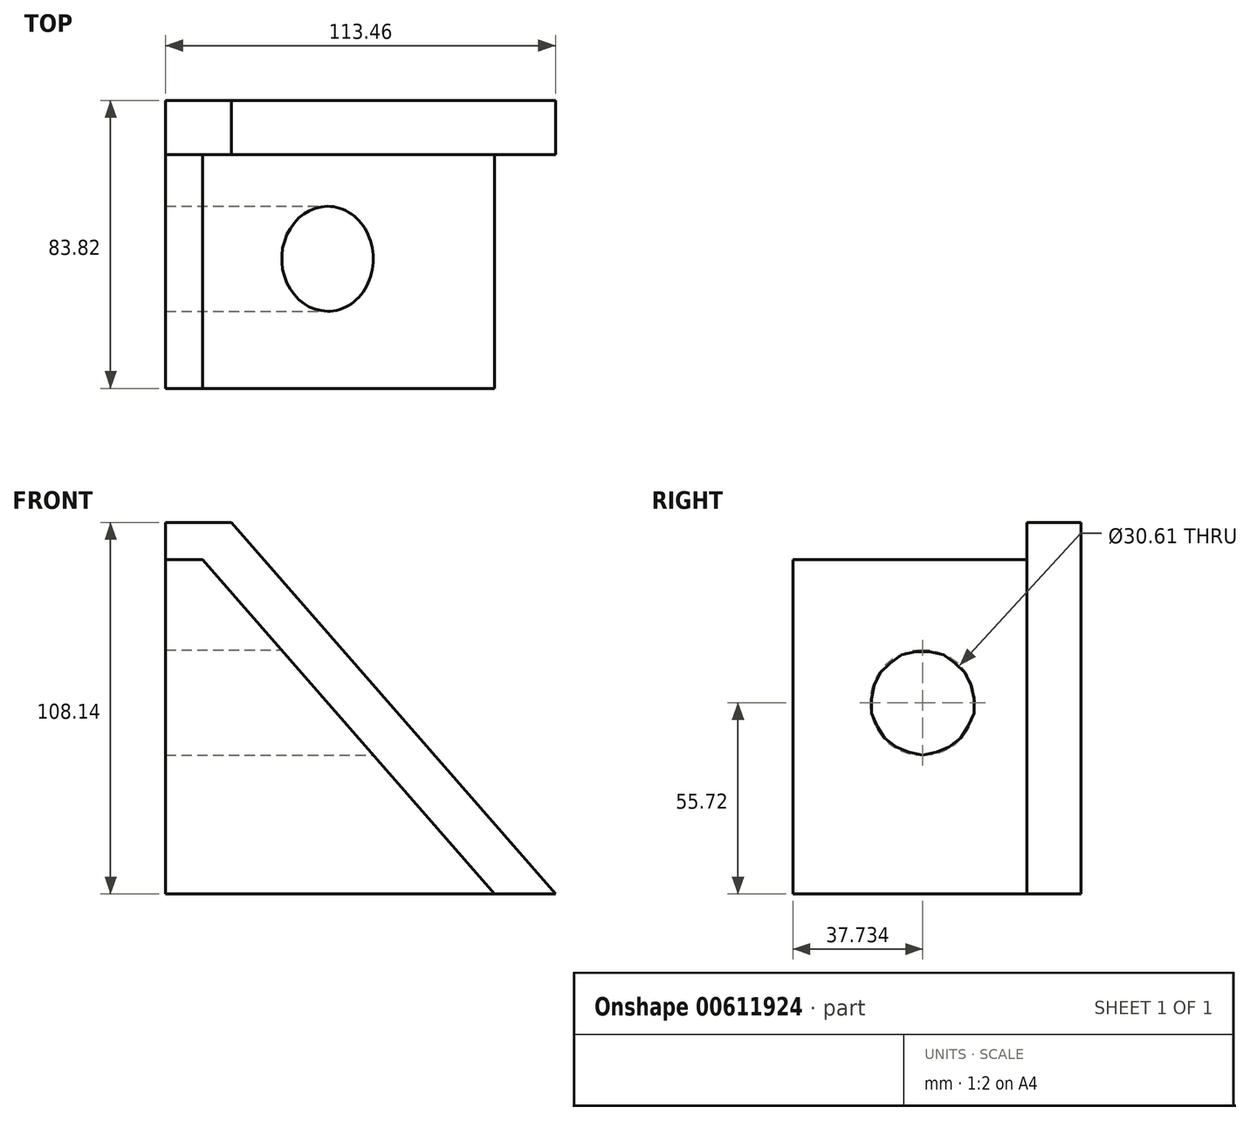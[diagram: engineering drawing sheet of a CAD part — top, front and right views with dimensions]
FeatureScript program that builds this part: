
annotation { "Feature Type Name" : "Feature", "Feature Type Description" : "" }
export const myFeature = defineFeature(function(context is Context, id is Id, definition is map)
    precondition{}
    {
        {
            var Q0;
            Q0=qCreatedBy(makeId("Front.planeOp"),FACE);
            var sketch = newSketch(context, id + "F0", { "sketchPlane" : qUnion([Q0])});
            skLineSegment(sketch, "E0.bottom", {"start": v(42.25, -40.14) * mm, "end": v(-53.43, -40.14) * mm});
            skLineSegment(sketch, "E0.top", {"start": v(42.25, 57.19) * mm, "end": v(-53.43, 57.19) * mm});
            skLineSegment(sketch, "E0.left", {"start": v(42.25, -40.14) * mm, "end": v(42.25, 57.19) * mm});
            skLineSegment(sketch, "E0.right", {"start": v(-53.43, -40.14) * mm, "end": v(-53.43, 57.19) * mm});
            skSolve(sketch);
        }
        {
            var Q0;
            Q0 = qSketchRegion(id + "F0", true);
            extrude(context, id + "F1", {"entities" : qUnion([Q0]), "depth" : 68.07 * mm, "offsetDistance" : 25.4 * mm});
        }
        {
            var Q0;
            Q0=makeQuery(id+"F1.opExtrude","CAP_FACE",FACE,{"disambiguationData":[OSD([sQuery(id+"F0.wireOp",EDGE,"E0.bottom"),sQuery(id+"F0.wireOp",EDGE,"E0.top"),sQuery(id+"F0.wireOp",EDGE,"E0.left"),sQuery(id+"F0.wireOp",EDGE,"E0.right")])],"isStart":true});
            var sketch = newSketch(context, id + "F2", { "sketchPlane" : qUnion([Q0])});
            skLineSegment(sketch, "E1.bottom", {"start": v(53.43, -40.14) * mm, "end": v(-60.03, -40.14) * mm});
            skLineSegment(sketch, "E1.top", {"start": v(53.43, 68) * mm, "end": v(-60.03, 68) * mm});
            skLineSegment(sketch, "E1.left", {"start": v(53.43, -40.14) * mm, "end": v(53.43, 68) * mm});
            skLineSegment(sketch, "E1.right", {"start": v(-60.03, -40.14) * mm, "end": v(-60.03, 68) * mm});
            skSolve(sketch);
        }
        {
            var Q0;
            Q0 = qSketchRegion(id + "F2", true);
            extrude(context, id + "F3", {"entities" : qUnion([Q0]), "operationType" : NewBodyOperationType.ADD, "depth" : 15.75 * mm, "offsetDistance" : 25.4 * mm});
        }
        {
            var Q0;
            Q0=makeQuery(id+"F1.opExtrude","SWEPT_FACE",FACE,{"disambiguationData":[OSD([sQuery(id+"F0.wireOp",EDGE,"E0.left")])]});
            var sketch = newSketch(context, id + "F4", { "sketchPlane" : qUnion([Q0])});
            skCircle(sketch, "E2", {"center": v(-30.34, 15.58) * mm, "radius": 15.3 * mm});
            skSolve(sketch);
        }
        {
            var Q0;
            Q0 = qSketchRegion(id + "F4", true);
            extrude(context, id + "F5", {"entities" : qUnion([Q0]), "operationType" : NewBodyOperationType.REMOVE, "oppositeDirection" : true, "depth" : 96.27 * mm, "offsetDistance" : 25.4 * mm});
        }
        {
            var Q0;
            Q0=makeQuery(id+"F1.opExtrude","CAP_FACE",FACE,{"disambiguationData":[OSD([sQuery(id+"F0.wireOp",EDGE,"E0.bottom"),sQuery(id+"F0.wireOp",EDGE,"E0.top"),sQuery(id+"F0.wireOp",EDGE,"E0.left"),sQuery(id+"F0.wireOp",EDGE,"E0.right")])],"isStart":false});
            var sketch = newSketch(context, id + "F6", { "sketchPlane" : qUnion([Q0])});
            skLineSegment(sketch, "E3", {"start": v(42.25, -40.14) * mm, "end": v(-42.62, 57.19) * mm});
            skLineSegment(sketch, "E4", {"start": v(-42.62, 57.19) * mm, "end": v(42.25, 57.19) * mm});
            skLineSegment(sketch, "E5", {"start": v(42.25, 57.19) * mm, "end": v(42.25, -40.14) * mm});
            skSolve(sketch);
        }
        {
            var Q0;
            Q0 = qSketchRegion(id + "F6", true);
            extrude(context, id + "F7", {"entities" : qUnion([Q0]), "operationType" : NewBodyOperationType.REMOVE, "oppositeDirection" : true, "depth" : 68.07 * mm, "offsetDistance" : 25.4 * mm});
        }
        {
            var Q0;
            Q0=makeQuery(id+"F7.boolean.opBoolean","MERGE",FACE,{"derivedFrom":[makeQuery(id+"F3.opExtrude","CAP_FACE",FACE,{"disambiguationData":[OSD([sQuery(id+"F2.wireOp",EDGE,"E1.bottom"),sQuery(id+"F2.wireOp",EDGE,"E1.top"),sQuery(id+"F2.wireOp",EDGE,"E1.left"),sQuery(id+"F2.wireOp",EDGE,"E1.right")])],"isStart":true}),makeQuery(id+"F7.opExtrude","CAP_FACE",FACE,{"disambiguationData":[OSD([sQuery(id+"F6.wireOp",EDGE,"E3"),sQuery(id+"F6.wireOp",EDGE,"E4"),sQuery(id+"F6.wireOp",EDGE,"E5")])],"isStart":false})]});
            var sketch = newSketch(context, id + "F8", { "sketchPlane" : qUnion([Q0])});
            skLineSegment(sketch, "E6", {"start": v(60.03, -40.14) * mm, "end": v(-34.27, 68) * mm});
            skLineSegment(sketch, "E7", {"start": v(-34.27, 68) * mm, "end": v(60.03, 68) * mm});
            skLineSegment(sketch, "E8", {"start": v(60.03, 68) * mm, "end": v(60.03, -40.14) * mm});
            skSolve(sketch);
        }
        {
            var Q0;
            Q0 = qSketchRegion(id + "F8", true);
            extrude(context, id + "F9", {"entities" : qUnion([Q0]), "operationType" : NewBodyOperationType.REMOVE, "oppositeDirection" : true, "depth" : 32.77 * mm, "offsetDistance" : 25.4 * mm});
        }
    });
